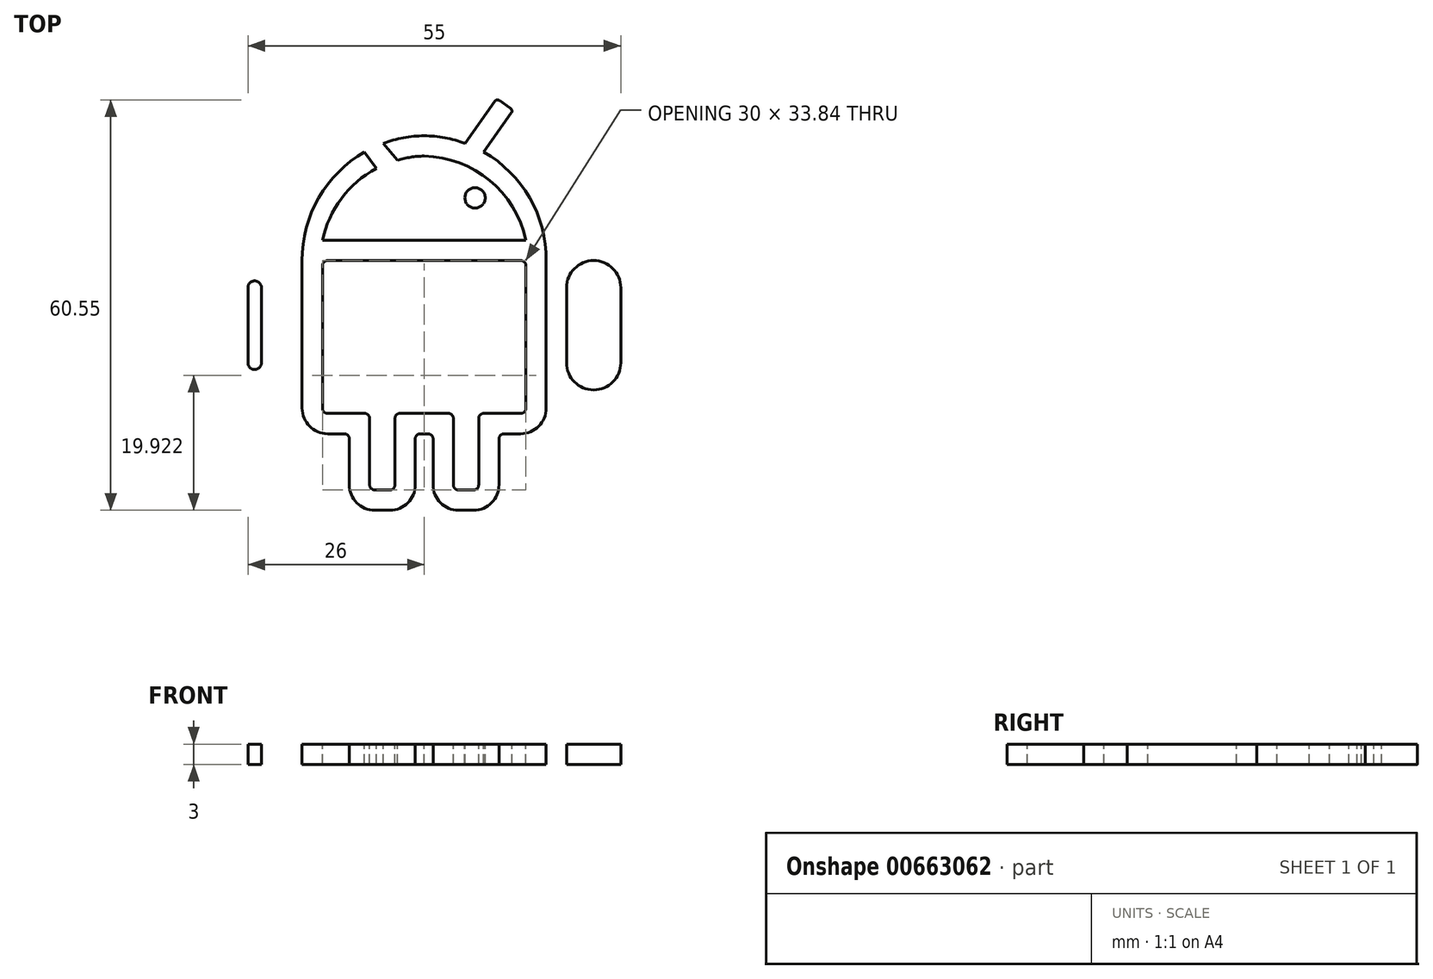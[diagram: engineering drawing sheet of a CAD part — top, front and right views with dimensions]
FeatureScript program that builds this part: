
annotation { "Feature Type Name" : "Feature", "Feature Type Description" : "" }
export const myFeature = defineFeature(function(context is Context, id is Id, definition is map)
    precondition{}
    {
        {
            var Q0;
            Q0=qCreatedBy(makeId("Top.planeOp"),FACE);
            var sketch = newSketch(context, id + "F0", { "sketchPlane" : qUnion([Q0])});
            skCircle(sketch, "E0", {"center": v(0, 0) * mm, "radius": 50 * mm});
            skSolve(sketch);
        }
        {
            assignVariable(context, id + "F1", {"name" : "Extrude", "anyValue" : 3 * mm});
        }
        {
            var Q0;
            Q0=qSketchRegion(id+"F0",true);
            extrude(context, id + "F2", {"entities" : qUnion([Q0]), "depth" : getVariable(context, 'Extrude'), "offsetDistance" : 25 * mm});
        }
        {
            assignVariable(context, id + "F3", {"name" : "Remove", "anyValue" : 3 * mm});
        }
        {
            var Q0;
            Q0=makeQuery(id+"F2.opExtrude","CAP_FACE",FACE,{"disambiguationData":[OSD([sQuery(id+"F0.wireOp",EDGE,"E0")])],"isStart":false});
            var sketch = newSketch(context, id + "F4", { "sketchPlane" : qUnion([Q0])});
            skLineSegment(sketch, "E1", {"start": v(0, 48) * mm, "end": v(0, -48) * mm, "construction": true});
            skLineSegment(sketch, "E2", {"start": v(-26, 0) * mm, "end": v(48, 0) * mm, "construction": true});
            skLineSegment(sketch, "E3", {"start": v(-26, 30.77) * mm, "end": v(26, -30.77) * mm, "construction": true});
            skLineSegment(sketch, "E4", {"start": v(26, 30.77) * mm, "end": v(-26, -30.77) * mm, "construction": true});
            skPoint(sketch, "E5", {"position": v(0, 0) * mm});
            skLineSegment(sketch, "E6", {"start": v(0, 6.77) * mm, "end": v(-14.25, 6.77) * mm});
            skLineSegment(sketch, "E7", {"start": v(-15, 6.02) * mm, "end": v(-15, -15.02) * mm});
            skLineSegment(sketch, "E8", {"start": v(-14.25, -15.77) * mm, "end": v(-8.8, -15.77) * mm});
            skLineSegment(sketch, "E9", {"start": v(-8.04, -16.52) * mm, "end": v(-8.04, -26.32) * mm});
            skLineSegment(sketch, "E10", {"start": v(-7.3, -27.07) * mm, "end": v(-5.06, -27.07) * mm});
            skLineSegment(sketch, "E11", {"start": v(-4.31, -26.32) * mm, "end": v(-4.31, -16.52) * mm});
            skLineSegment(sketch, "E12", {"start": v(-3.56, -15.77) * mm, "end": v(0, -15.77) * mm});
            skLineSegment(sketch, "E13", {"start": v(0, 9.77) * mm, "end": v(-15, 9.77) * mm});
            skPoint(sketch, "E14.visualSharp", {"position": v(-15, 6.77) * mm});
            skArc(sketch, "E14.filletArc", {"start": v(-14.25, 6.77) * mm, "mid": v(-14.78, 6.55) * mm, "end": v(-15, 6.02) * mm});
            skPoint(sketch, "E15.visualSharp", {"position": v(-15, -15.77) * mm});
            skArc(sketch, "E15.filletArc", {"start": v(-15, -15.02) * mm, "mid": v(-14.78, -15.55) * mm, "end": v(-14.25, -15.77) * mm});
            skPoint(sketch, "E16.visualSharp", {"position": v(-8.04, -15.77) * mm});
            skArc(sketch, "E16.filletArc", {"start": v(-8.04, -16.52) * mm, "mid": v(-8.26, -16) * mm, "end": v(-8.8, -15.77) * mm});
            skPoint(sketch, "E17.visualSharp", {"position": v(-8.04, -27.07) * mm});
            skArc(sketch, "E17.filletArc", {"start": v(-8.04, -26.32) * mm, "mid": v(-7.82, -26.85) * mm, "end": v(-7.3, -27.07) * mm});
            skPoint(sketch, "E18.visualSharp", {"position": v(-4.31, -27.07) * mm});
            skArc(sketch, "E18.filletArc", {"start": v(-5.06, -27.07) * mm, "mid": v(-4.53, -26.85) * mm, "end": v(-4.31, -26.32) * mm});
            skArc(sketch, "E19", {"start": v(0, 22.2) * mm, "mid": v(-9.67, 18.6) * mm, "end": v(-15, 9.77) * mm});
            skPoint(sketch, "E20.visualSharp", {"position": v(-4.31, -15.77) * mm});
            skArc(sketch, "E20.filletArc", {"start": v(-3.56, -15.77) * mm, "mid": v(-4.1, -16) * mm, "end": v(-4.31, -16.52) * mm});
            skCircle(sketch, "E21", {"center": v(-7.5, 16.03) * mm, "radius": 1.5 * mm});
            skLineSegment(sketch, "E22", {"start": v(-6, 17.53) * mm, "end": v(-6, 16.37) * mm, "construction": true});
            skLineSegment(sketch, "E23", {"start": v(-6, 17.53) * mm, "end": v(-8.55, 17.53) * mm, "construction": true});
            skLineSegment(sketch, "E24.0", {"start": v(-0.56, -18.77) * mm, "end": v(0, -18.77) * mm});
            skLineSegment(sketch, "E24.1", {"start": v(-1.31, -26.32) * mm, "end": v(-1.31, -19.52) * mm});
            skLineSegment(sketch, "E24.2", {"start": v(-11.04, -19.52) * mm, "end": v(-11.04, -26.32) * mm});
            skArc(sketch, "E24.3", {"start": v(-11.04, -26.32) * mm, "mid": v(-9.94, -28.97) * mm, "end": v(-7.3, -30.07) * mm});
            skLineSegment(sketch, "E24.4", {"start": v(-7.3, -30.07) * mm, "end": v(-5.06, -30.07) * mm});
            skArc(sketch, "E24.5", {"start": v(-5.06, -30.07) * mm, "mid": v(-2.41, -28.97) * mm, "end": v(-1.31, -26.32) * mm});
            skLineSegment(sketch, "E25.0", {"start": v(-14.25, -18.77) * mm, "end": v(-11.8, -18.77) * mm});
            skLineSegment(sketch, "E25.3", {"start": v(-18, 6.77) * mm, "end": v(-18, -15.02) * mm});
            skArc(sketch, "E25.4", {"start": v(-18, -15.02) * mm, "mid": v(-16.9, -17.68) * mm, "end": v(-14.25, -18.77) * mm});
            skPoint(sketch, "E26.visualSharp", {"position": v(-11.04, -18.77) * mm});
            skArc(sketch, "E26.filletArc", {"start": v(-11.04, -19.52) * mm, "mid": v(-11.26, -19) * mm, "end": v(-11.8, -18.77) * mm});
            skArc(sketch, "E27", {"start": v(0, 25.2) * mm, "mid": v(-3.06, 24.89) * mm, "end": v(-6.03, 24.07) * mm});
            skLineSegment(sketch, "E28", {"start": v(-8.8, 22.79) * mm, "end": v(-12.85, 28.54) * mm});
            skLineSegment(sketch, "E29", {"start": v(-12.73, 29.23) * mm, "end": v(-11.1, 30.39) * mm});
            skLineSegment(sketch, "E30", {"start": v(-10.4, 30.27) * mm, "end": v(-6.03, 24.07) * mm});
            skPoint(sketch, "E31.visualSharp", {"position": v(-13.14, 28.95) * mm});
            skArc(sketch, "E31.filletArc", {"start": v(-12.73, 29.23) * mm, "mid": v(-12.93, 28.9) * mm, "end": v(-12.85, 28.54) * mm});
            skPoint(sketch, "E32.visualSharp", {"position": v(-10.69, 30.67) * mm});
            skArc(sketch, "E32.filletArc", {"start": v(-10.4, 30.27) * mm, "mid": v(-10.72, 30.47) * mm, "end": v(-11.1, 30.39) * mm});
            skArc(sketch, "E33", {"start": v(-8.8, 22.79) * mm, "mid": v(-15.57, 16.03) * mm, "end": v(-18, 6.77) * mm});
            skArc(sketch, "E34", {"start": v(-6.03, 24.07) * mm, "mid": v(-7.44, 23.49) * mm, "end": v(-8.8, 22.79) * mm, "construction": true});
            skLineSegment(sketch, "E35.left", {"start": v(-21, 2.77) * mm, "end": v(-21, -8.3) * mm});
            skLineSegment(sketch, "E35.right", {"start": v(-29, 2.77) * mm, "end": v(-29, -8.3) * mm});
            skPoint(sketch, "E36.orphan", {"position": v(-48, 0) * mm});
            skArc(sketch, "E37", {"start": v(-21, 2.77) * mm, "mid": v(-25, 6.77) * mm, "end": v(-29, 2.77) * mm});
            skArc(sketch, "E38", {"start": v(-29, -8.3) * mm, "mid": v(-25, -12.3) * mm, "end": v(-21, -8.3) * mm});
            skPoint(sketch, "E39", {"position": v(-25, 6.77) * mm});
            skLineSegment(sketch, "E40.0", {"start": v(-26, 2.77) * mm, "end": v(-26, -8.3) * mm});
            skArc(sketch, "E40.1", {"start": v(-24, 2.77) * mm, "mid": v(-25, 3.77) * mm, "end": v(-26, 2.77) * mm});
            skLineSegment(sketch, "E40.2", {"start": v(-24, 2.77) * mm, "end": v(-24, -8.3) * mm});
            skArc(sketch, "E40.3", {"start": v(-26, -8.3) * mm, "mid": v(-25, -9.3) * mm, "end": v(-24, -8.3) * mm});
            skArc(sketch, "E41.MirrorCS", {"start": v(8.8, 22.79) * mm, "mid": v(15.57, 16.03) * mm, "end": v(18, 6.77) * mm});
            skArc(sketch, "E42.MirrorCS", {"start": v(10.4, 30.27) * mm, "mid": v(10.72, 30.47) * mm, "end": v(11.1, 30.39) * mm});
            skArc(sketch, "E43.MirrorCS", {"start": v(12.73, 29.23) * mm, "mid": v(12.93, 28.9) * mm, "end": v(12.85, 28.54) * mm});
            skLineSegment(sketch, "E44.MirrorCS", {"start": v(12.73, 29.23) * mm, "end": v(11.1, 30.39) * mm});
            skLineSegment(sketch, "E45.MirrorCS", {"start": v(10.4, 30.27) * mm, "end": v(6.03, 24.07) * mm});
            skLineSegment(sketch, "E46.MirrorCS", {"start": v(8.8, 22.79) * mm, "end": v(12.85, 28.54) * mm});
            skArc(sketch, "E47.MirrorCS", {"start": v(0, 22.2) * mm, "mid": v(9.67, 18.6) * mm, "end": v(15, 9.77) * mm});
            skArc(sketch, "E48.MirrorCS", {"start": v(0, 25.2) * mm, "mid": v(3.06, 24.89) * mm, "end": v(6.03, 24.07) * mm});
            skArc(sketch, "E49.MirrorCS", {"start": v(14.25, 6.77) * mm, "mid": v(14.78, 6.55) * mm, "end": v(15, 6.02) * mm});
            skLineSegment(sketch, "E50.MirrorCS", {"start": v(0, 9.77) * mm, "end": v(15, 9.77) * mm});
            skLineSegment(sketch, "E51.MirrorCS", {"start": v(0, 6.77) * mm, "end": v(14.25, 6.77) * mm});
            skLineSegment(sketch, "E52.MirrorCS", {"start": v(15, 6.02) * mm, "end": v(15, -15.02) * mm});
            skLineSegment(sketch, "E53.MirrorCS", {"start": v(18, 6.77) * mm, "end": v(18, -15.02) * mm});
            skArc(sketch, "E54.MirrorCS", {"start": v(18, -15.02) * mm, "mid": v(16.9, -17.68) * mm, "end": v(14.25, -18.77) * mm});
            skArc(sketch, "E55.MirrorCS", {"start": v(15, -15.02) * mm, "mid": v(14.78, -15.55) * mm, "end": v(14.25, -15.77) * mm});
            skLineSegment(sketch, "E56.MirrorCS", {"start": v(14.25, -15.77) * mm, "end": v(8.8, -15.77) * mm});
            skLineSegment(sketch, "E57.MirrorCS", {"start": v(14.25, -18.77) * mm, "end": v(11.8, -18.77) * mm});
            skArc(sketch, "E58.MirrorCS", {"start": v(8.04, -16.52) * mm, "mid": v(8.26, -16) * mm, "end": v(8.8, -15.77) * mm});
            skArc(sketch, "E59.MirrorCS", {"start": v(11.04, -19.52) * mm, "mid": v(11.26, -19) * mm, "end": v(11.8, -18.77) * mm});
            skLineSegment(sketch, "E60.MirrorCS", {"start": v(11.04, -19.52) * mm, "end": v(11.04, -26.32) * mm});
            skLineSegment(sketch, "E61.MirrorCS", {"start": v(8.04, -16.52) * mm, "end": v(8.04, -26.32) * mm});
            skArc(sketch, "E62.MirrorCS", {"start": v(11.04, -26.32) * mm, "mid": v(9.94, -28.97) * mm, "end": v(7.3, -30.07) * mm});
            skArc(sketch, "E63.MirrorCS", {"start": v(8.04, -26.32) * mm, "mid": v(7.82, -26.85) * mm, "end": v(7.3, -27.07) * mm});
            skLineSegment(sketch, "E64.MirrorCS", {"start": v(7.3, -30.07) * mm, "end": v(5.06, -30.07) * mm});
            skLineSegment(sketch, "E65.MirrorCS", {"start": v(7.3, -27.07) * mm, "end": v(5.06, -27.07) * mm});
            skArc(sketch, "E66.MirrorCS", {"start": v(5.06, -30.07) * mm, "mid": v(2.41, -28.97) * mm, "end": v(1.31, -26.32) * mm});
            skArc(sketch, "E67.MirrorCS", {"start": v(5.06, -27.07) * mm, "mid": v(4.53, -26.85) * mm, "end": v(4.31, -26.32) * mm});
            skLineSegment(sketch, "E68.MirrorCS", {"start": v(4.31, -26.32) * mm, "end": v(4.31, -16.52) * mm});
            skLineSegment(sketch, "E69.MirrorCS", {"start": v(1.31, -26.32) * mm, "end": v(1.31, -19.52) * mm});
            skLineSegment(sketch, "E70.MirrorCS", {"start": v(3.56, -15.77) * mm, "end": v(0, -15.77) * mm});
            skArc(sketch, "E71.MirrorCS", {"start": v(3.56, -15.77) * mm, "mid": v(4.1, -16) * mm, "end": v(4.31, -16.52) * mm});
            skLineSegment(sketch, "E72.MirrorCS", {"start": v(0.56, -18.77) * mm, "end": v(0, -18.77) * mm});
            skArc(sketch, "E73.MirrorCS", {"start": v(29, -8.3) * mm, "mid": v(25, -12.3) * mm, "end": v(21, -8.3) * mm});
            skArc(sketch, "E74.MirrorCS", {"start": v(26, -8.3) * mm, "mid": v(25, -9.3) * mm, "end": v(24, -8.3) * mm});
            skLineSegment(sketch, "E75.MirrorCS", {"start": v(26, 2.77) * mm, "end": v(26, -8.3) * mm});
            skLineSegment(sketch, "E76.MirrorCS", {"start": v(29, 2.77) * mm, "end": v(29, -8.3) * mm});
            skLineSegment(sketch, "E77.MirrorCS", {"start": v(24, 2.77) * mm, "end": v(24, -8.3) * mm});
            skLineSegment(sketch, "E78.MirrorCS", {"start": v(21, 2.77) * mm, "end": v(21, -8.3) * mm});
            skArc(sketch, "E79.MirrorCS", {"start": v(24, 2.77) * mm, "mid": v(25, 3.77) * mm, "end": v(26, 2.77) * mm});
            skArc(sketch, "E80.MirrorCS", {"start": v(21, 2.77) * mm, "mid": v(25, 6.77) * mm, "end": v(29, 2.77) * mm});
            skPoint(sketch, "E81.visualSharp", {"position": v(-1.31, -18.77) * mm});
            skArc(sketch, "E81.filletArc", {"start": v(-0.56, -18.77) * mm, "mid": v(-1.1, -19) * mm, "end": v(-1.31, -19.52) * mm});
            skPoint(sketch, "E82.visualSharp", {"position": v(1.31, -18.77) * mm});
            skArc(sketch, "E82.filletArc", {"start": v(1.31, -19.52) * mm, "mid": v(1.1, -19) * mm, "end": v(0.56, -18.77) * mm});
            skCircle(sketch, "E83.MirrorC", {"center": v(7.5, 16.03) * mm, "radius": 1.5 * mm});
            skLineSegment(sketch, "E84", {"start": v(-8.8, 22.79) * mm, "end": v(-7.08, 20.35) * mm});
            skLineSegment(sketch, "E85", {"start": v(-6.03, 24.07) * mm, "end": v(-3.95, 21.6) * mm});
            skSolve(sketch);
        }
        {
            var Q0;
            Q0=makeQuery(id+"F4.imprint","IMPRINT",FACE,{"disambiguationData":[TD([[makeQuery(id+"F4.imprint","IMPRINT",EDGE,{"derivedFrom":sQuery(id+"F4.wireOp",EDGE,"E13")}),-1.0]])]});
            var Q1;
            Q1=makeQuery(id+"F4.imprint","IMPRINT",FACE,{"disambiguationData":[TD([[makeQuery(id+"F4.imprint","IMPRINT",EDGE,{"derivedFrom":sQuery(id+"F4.wireOp",EDGE,"E21")}),1.0]])]});
            var Q2;
            Q2=makeQuery(id+"F4.imprint","IMPRINT",FACE,{"disambiguationData":[TD([[makeQuery(id+"F4.imprint","IMPRINT",EDGE,{"derivedFrom":sQuery(id+"F4.wireOp",EDGE,"E83.MirrorC")}),-1.0]])]});
            var Q3;
            Q3=makeQuery(id+"F4.imprint","IMPRINT",FACE,{"disambiguationData":[TD([[makeQuery(id+"F4.imprint","IMPRINT",EDGE,{"derivedFrom":sQuery(id+"F4.wireOp",EDGE,"E73.MirrorCS")}),-1.0]])]});
            var Q4;
            Q4=makeQuery(id+"F4.imprint","IMPRINT",FACE,{"disambiguationData":[TD([[makeQuery(id+"F4.imprint","IMPRINT",EDGE,{"derivedFrom":sQuery(id+"F4.wireOp",EDGE,"E35.left")}),-1.0]])]});
            var Q5;
            Q5=makeQuery(id+"F4.imprint","IMPRINT",FACE,{"disambiguationData":[TD([[makeQuery(id+"F4.imprint","IMPRINT",EDGE,{"derivedFrom":sQuery(id+"F4.wireOp",EDGE,"E6")}),1.0]])]});
            var Q6;
            Q6=makeQuery(id+"F4.imprint","IMPRINT",FACE,{"disambiguationData":[TD([[makeQuery(id+"F4.imprint","IMPRINT",EDGE,{"derivedFrom":sQuery(id+"F4.wireOp",EDGE,"E28")}),-1.0]])]});
            extrude(context, id + "F5", {"entities" : qUnion([Q0, Q1, Q2, Q3, Q4, Q5, Q6]), "operationType" : NewBodyOperationType.REMOVE, "oppositeDirection" : true, "depth" : getVariable(context, 'Remove'), "offsetDistance" : 25 * mm});
        }
        {
            var Q0;
            Q0=makeQuery(id+"F4.imprint","IMPRINT",FACE,{"disambiguationData":[TD([[makeQuery(id+"F4.imprint","IMPRINT",EDGE,{"derivedFrom":sQuery(id+"F4.wireOp",EDGE,"E21")}),1.0]])]});
            var Q1;
            Q1=makeQuery(id+"F4.imprint","IMPRINT",FACE,{"disambiguationData":[TD([[makeQuery(id+"F4.imprint","IMPRINT",EDGE,{"derivedFrom":sQuery(id+"F4.wireOp",EDGE,"E83.MirrorC")}),-1.0]])]});
            extrude(context, id + "F6", {"entities" : qUnion([Q0, Q1]), "operationType" : NewBodyOperationType.REMOVE, "oppositeDirection" : true, "depth" : getVariable(context, 'Remove'), "offsetDistance" : 25 * mm});
        }
    });
